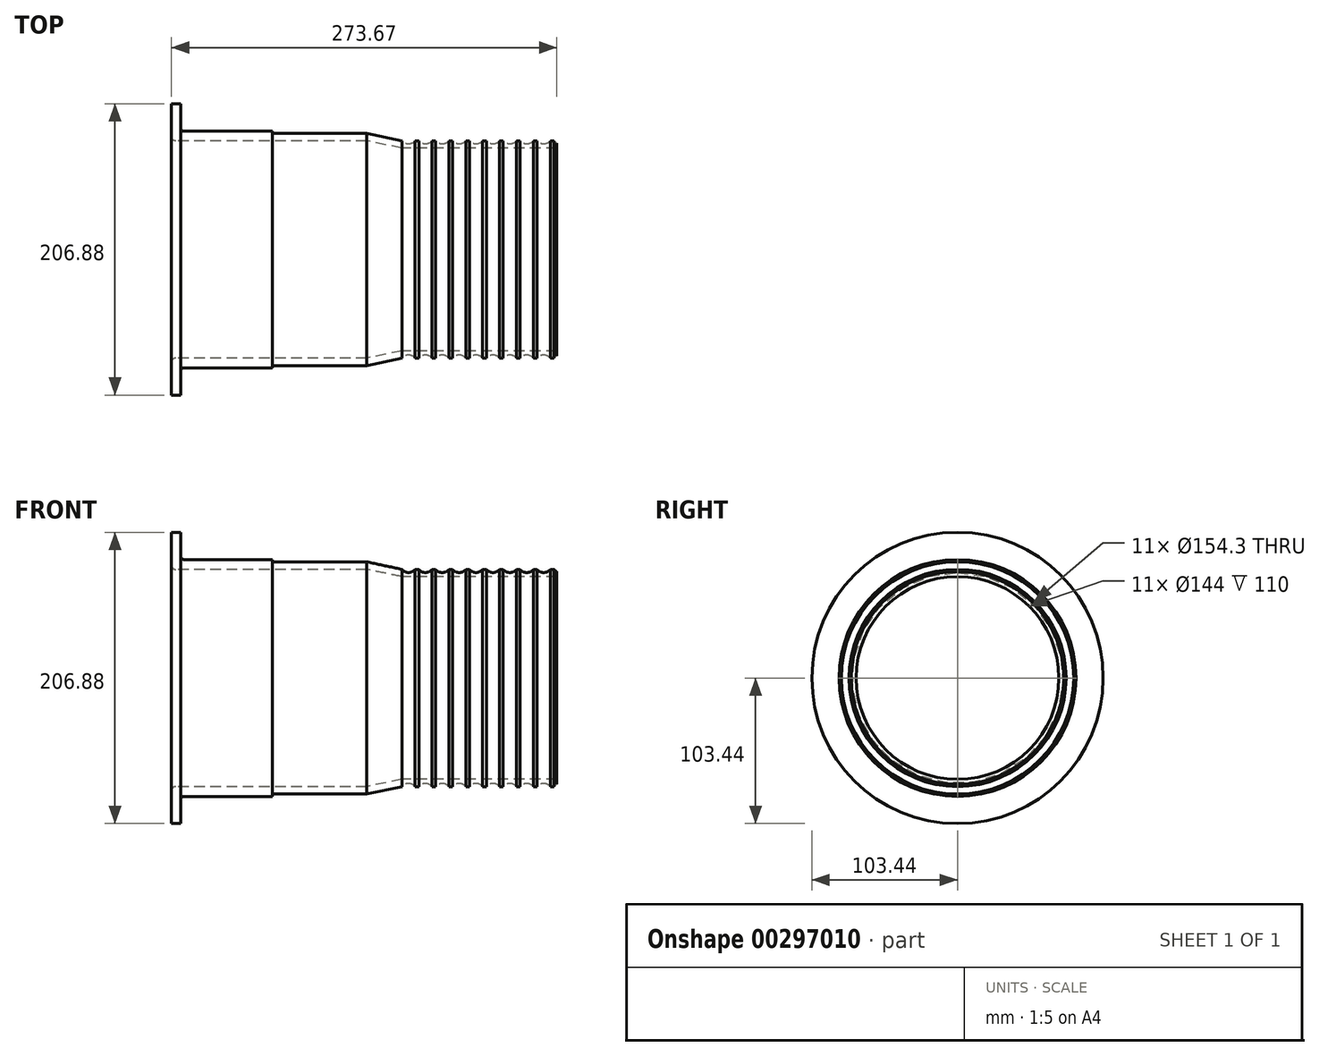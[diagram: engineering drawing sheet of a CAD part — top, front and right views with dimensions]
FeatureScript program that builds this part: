
annotation { "Feature Type Name" : "Feature", "Feature Type Description" : "" }
export const myFeature = defineFeature(function(context is Context, id is Id, definition is map)
    precondition{}
    {
        {
            var Q0;
            Q0=qCreatedBy(makeId("Front.planeOp"),FACE);
            var sketch = newSketch(context, id + "F0", { "sketchPlane" : qUnion([Q0])});
            skLineSegment(sketch, "E0", {"start": v(0, 0) * mm, "end": v(135, 0) * mm});
            skLineSegment(sketch, "E1", {"start": v(135, 0) * mm, "end": v(160, -5.15) * mm});
            skLineSegment(sketch, "E2", {"start": v(160, -5.15) * mm, "end": v(270, -5.15) * mm});
            skLineSegment(sketch, "E3", {"start": v(5, 7) * mm, "end": v(68, 7) * mm});
            skLineSegment(sketch, "E4", {"start": v(68, 7) * mm, "end": v(68, 5.35) * mm});
            skLineSegment(sketch, "E5", {"start": v(68, 5.35) * mm, "end": v(135, 5.35) * mm});
            skLineSegment(sketch, "E6", {"start": v(135, 5.35) * mm, "end": v(160, 0) * mm, "construction": true});
            skLineSegment(sketch, "E7", {"start": v(160, -20.32) * mm, "end": v(160, 17.36) * mm, "construction": true});
            skLineSegment(sketch, "E8", {"start": v(270, -5.15) * mm, "end": v(270, 59.01) * mm, "construction": true});
            skLineSegment(sketch, "E9", {"start": v(270, -0.24) * mm, "end": v(270, -5.15) * mm});
            skArc(sketch, "E10", {"start": v(160, 0) * mm, "mid": v(164.68, -2.25) * mm, "end": v(169.37, 0) * mm});
            skPoint(sketch, "E11.endSnap0", {"position": v(164.68, -2.25) * mm});
            skArc(sketch, "E12.1.0.0", {"start": v(172, 0) * mm, "mid": v(176.68, -2.25) * mm, "end": v(181.37, 0) * mm});
            skArc(sketch, "E12.2.0.0", {"start": v(184, 0) * mm, "mid": v(188.68, -2.25) * mm, "end": v(193.37, 0) * mm});
            skArc(sketch, "E12.3.0.0", {"start": v(196, 0) * mm, "mid": v(200.68, -2.25) * mm, "end": v(205.37, 0) * mm});
            skArc(sketch, "E12.4.0.0", {"start": v(208, 0) * mm, "mid": v(212.68, -2.25) * mm, "end": v(217.37, 0) * mm});
            skArc(sketch, "E12.5.0.0", {"start": v(220, 0) * mm, "mid": v(224.68, -2.25) * mm, "end": v(229.37, 0) * mm});
            skArc(sketch, "E12.6.0.0", {"start": v(232, 0) * mm, "mid": v(236.68, -2.25) * mm, "end": v(241.37, 0) * mm});
            skArc(sketch, "E12.7.0.0", {"start": v(244, 0) * mm, "mid": v(248.68, -2.25) * mm, "end": v(253.37, 0) * mm});
            skArc(sketch, "E12.8.0.0", {"start": v(256, 0) * mm, "mid": v(260.68, -2.25) * mm, "end": v(265.37, 0) * mm});
            skLineSegment(sketch, "E13", {"start": v(169.37, 0) * mm, "end": v(172, 0) * mm});
            skLineSegment(sketch, "E14.1.0.0", {"start": v(181.37, 0) * mm, "end": v(184, 0) * mm});
            skLineSegment(sketch, "E14.2.0.0", {"start": v(193.37, 0) * mm, "end": v(196, 0) * mm});
            skLineSegment(sketch, "E14.3.0.0", {"start": v(205.37, 0) * mm, "end": v(208, 0) * mm});
            skLineSegment(sketch, "E14.4.0.0", {"start": v(217.37, 0) * mm, "end": v(220, 0) * mm});
            skLineSegment(sketch, "E14.5.0.0", {"start": v(229.37, 0) * mm, "end": v(232, 0) * mm});
            skLineSegment(sketch, "E14.6.0.0", {"start": v(241.37, 0) * mm, "end": v(244, 0) * mm});
            skLineSegment(sketch, "E14.7.0.0", {"start": v(253.37, 0) * mm, "end": v(256, 0) * mm});
            skLineSegment(sketch, "E14.8.0.0", {"start": v(265.37, 0) * mm, "end": v(268, 0) * mm});
            skLineSegment(sketch, "E15", {"start": v(135, 0) * mm, "end": v(135, 19.01) * mm, "construction": true});
            skLineSegment(sketch, "E16", {"start": v(135, 5.35) * mm, "end": v(160, 0) * mm});
            skLineSegment(sketch, "E17", {"start": v(-11.74, -77.15) * mm, "end": v(291.26, -77.15) * mm, "construction": true});
            skArc(sketch, "E18.1.0.0", {"start": v(268, 0) * mm, "mid": v(268.91, -0.92) * mm, "end": v(270, -1.62) * mm});
            skPoint(sketch, "E19.orphan", {"position": v(277.37, 0) * mm});
            skLineSegment(sketch, "E20", {"start": v(3, 9) * mm, "end": v(3, 26.29) * mm});
            skLineSegment(sketch, "E21", {"start": v(3, 26.29) * mm, "end": v(-3.67, 26.29) * mm});
            skLineSegment(sketch, "E22", {"start": v(-3.67, 26.29) * mm, "end": v(-3.67, 3) * mm});
            skLineSegment(sketch, "E23", {"start": v(-0.67, 0) * mm, "end": v(0, 0) * mm});
            skPoint(sketch, "E24.visualSharp", {"position": v(3, 7) * mm});
            skArc(sketch, "E24.filletArc", {"start": v(3, 9) * mm, "mid": v(3.59, 7.59) * mm, "end": v(5, 7) * mm});
            skPoint(sketch, "E25.visualSharp", {"position": v(-3.67, 0) * mm});
            skArc(sketch, "E25.filletArc", {"start": v(-3.67, 3) * mm, "mid": v(-2.79, 0.88) * mm, "end": v(-0.67, 0) * mm});
            skSolve(sketch);
        }
        {
            var Q0;
            Q0=makeQuery(id+"F0.imprint","IMPRINT",FACE,{"disambiguationData":[TD([[makeQuery(id+"F0.imprint","IMPRINT",EDGE,{"derivedFrom":sQuery(id+"F0.wireOp",EDGE,"E0")}),1.0]])]});
            var Q1;
            Q1=sQuery(id+"F0.wireOp",EDGE,"E17");
            revolve(context, id + "F1", {"entities" : qUnion([Q0]), "axis" : qUnion([Q1]), "revolveType" : RevolveType.FULL});
        }
    });
